# Revit family: Elkay_Drinking-Water_Bottle-Filling-Stations_VRC_Onwall_St1_Asiapac
name_source: partatom
category: Plumbing Fixtures
units: mm (PartAtom-declared; Revit-internal decimal feet)

## family parameters
Always vertical = Yes
Cut with Voids When Loaded = No
Part Type = Normal
Room Calculation Point = No
Round Connector Dimension = Use Diameter
Shared = No
Work Plane-Based = No

## types (9) — shared parameters
Activation by = Electronic Bottle Filler Button With Mechanical Front Bubbler Button
Body_Finish = 304 Stainless Steel
Bubbler Style = Vandal Resistant
CW Connection = No
Dimensions (L x W x H) = 18 inch x 18 5/8 inch x 38 13/16 inch
Finish = Stainless Steel
Manufacturer = Elkay
Mounting Type = Wall Mount (On Wall)
Number of Stations = 1
Version = 1.0.0.0

## per-type parameters (varying)
| type | Approx. Shipping Weight | Chilling Capacity | Full Load Amps | Installation Location | Power | Rated Watts | Special Features |
| LVRC8WS3KSA | 88 lbs | 8.0 GPH | 3.2 | Indoor | 220V/60Hz | 370 | Visual Filter Monitor, Filtered, Green Ticker™, Laminar Flow, Real Drain, Vandal Resistant |
| LVRC8WS2K | 91 lbs | 8.0 GPH | 3 | Indoor | 220V/50Hz | 370 | Filtered, Green Ticker™, Laminar Flow, Real Drain, Vandal Resistant,Visual Filter Monitor |
| LVRC8WS3K | 91 lbs | 8.0 GPH | 3.2 | Indoor | 220V/60Hz | 370 | Visual Filter Monitor, Filtered, Green Ticker™, Laminar Flow, Real Drain, Vandal Resistant |
| LVRCDWS2K | 59 lbs | Non-refrigerated | 1 | Indoor | 220V/50Hz | 15 | Visual Filter Monitor, Filtered, Green Ticker™, Laminar Flow, Real Drain, Vandal Resistant |
| LVRCDWS3K | 59 lbs | Non-refrigerated | 1 | Indoor | 220V/60Hz | 15 | Visual Filter Monitor, Filtered, Green Ticker™, Laminar Flow, Real Drain, Vandal Resistant |
| VRC8WS2K | 87 lbs | 8.0 GPH | 3 | Indoor + Outdoor | 220V/50Hz | 370 | Green Ticker™, Laminar Flow, Real Drain, Vandal Resistant |
| VRC8WS3K | 87 lbs | 8.0 GPH | 3.2 | Indoor + Outdoor | 220V/60Hz | 370 | Green Ticker™, Laminar Flow, Real Drain, Vandal Resistant |
| VRCDWS2K | 56 lbs | Non-refrigerated | 1 | Indoor + Outdoor | 220V/50Hz | 15 | Green Ticker™, Laminar Flow, Real Drain, Vandal Resistant |
| VRCDWS3K | 56 lbs | Non-refrigerated | 1 | Indoor + Outdoor | 220V/60Hz | 15 | Green Ticker™, Laminar Flow, Real Drain, Vandal Resistant |

note: column(s) folded — value = type name in every type: Model

## geometry (parser evidence)
native form markers: Sweep x27
no freeform markers — native parametric forms only
